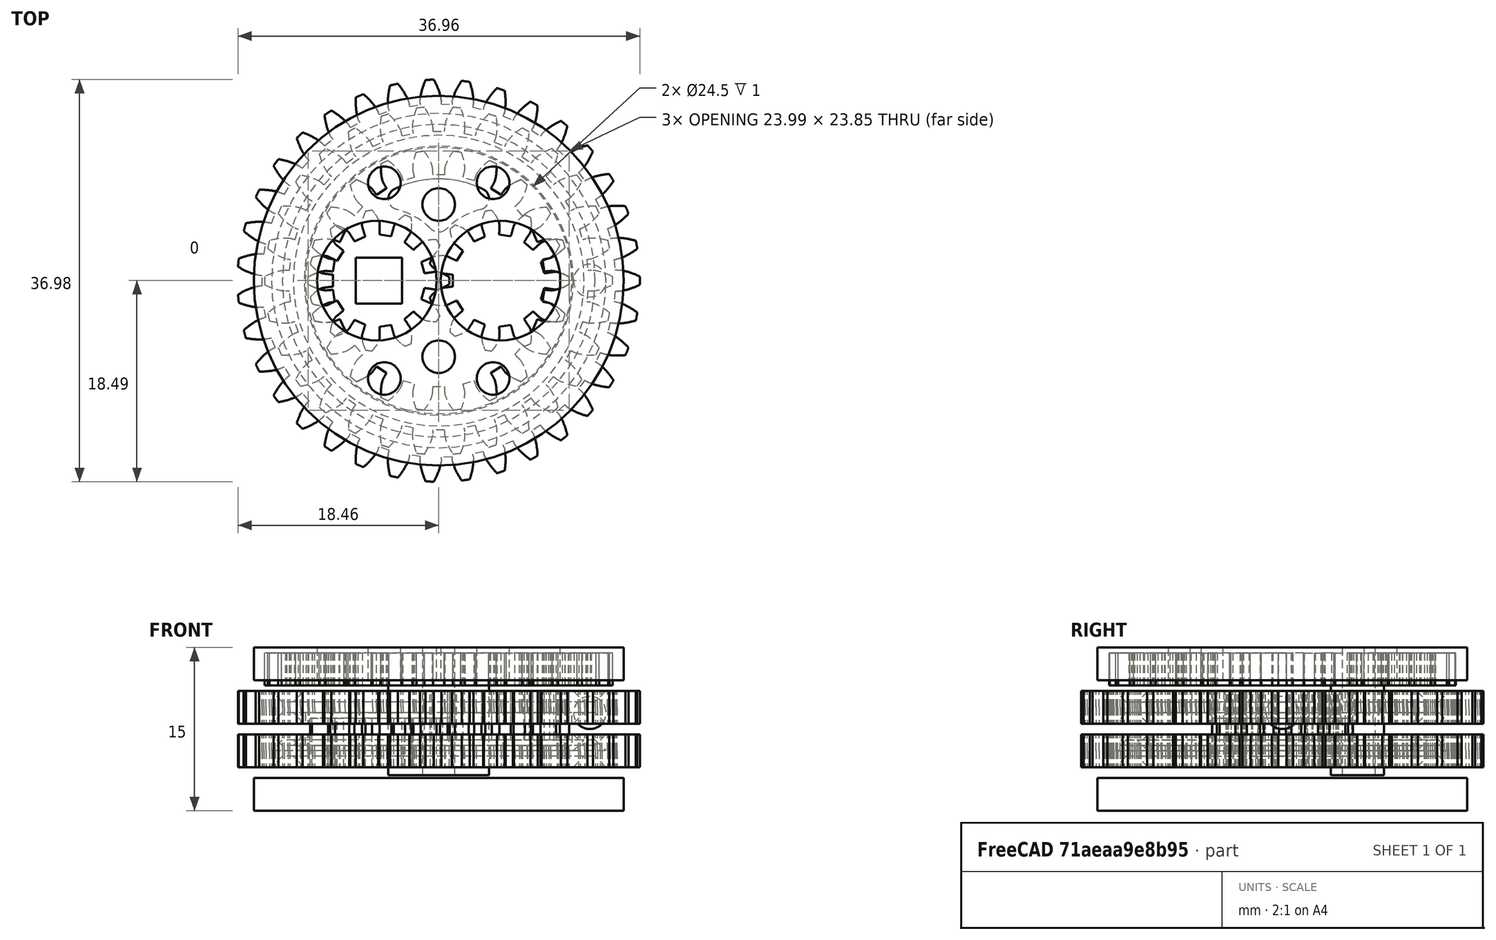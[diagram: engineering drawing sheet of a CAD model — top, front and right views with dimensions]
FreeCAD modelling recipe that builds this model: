
FCSTD DOCUMENT  (FreeCAD 0.16RUnknown)
Label: PlanetaryDifferential
License: CreativeCommons Attribution-NonCommercial
LicenseURL: http://creativecommons.org/licenses/by-nc/4.0/
objects: Sketcher::SketchObject×8, PartDesign::Pad×5, Part::FeaturePython×4, Part::Cut×4, PartDesign::Revolution×2, Part::Feature×2, Part::Sphere×1, Mesh::Feature×1, PartDesign::Fillet×1, Part::Mirroring×1, Part::MultiFuse×1
note: 36 computed .brp shape members not serialized (recipe doc carries the construction recipe); baked Part::Feature solids carry a one-line shape summary decoded from their .brp

FEATURE [Sketcher::SketchObject] Sketch
  sketch-geometry (3):
    g0: Circle CenterX=0 CenterY=0 CenterZ=0 NormalX=0 NormalY=0 NormalZ=1 Radius=36.0346
    g1: Circle CenterX=-36.0346 CenterY=0 CenterZ=0 NormalX=0 NormalY=0 NormalZ=1 Radius=36.0346
    g2: Circle CenterX=36.0346 CenterY=0 CenterZ=0 NormalX=0 NormalY=0 NormalZ=1 Radius=36.0346
  constraints (7):
    c: Coincident(g0,g-1)
    c: PointOnObject(g1,g0)
    c: PointOnObject(g2,g0)
    c: PointOnObject(g2,g-1)
    c: PointOnObject(g1,g-1)
    c: Equal(g0,g1)
    c: Equal(g1,g2)
FEATURE [Part::FeaturePython] InvoluteGear  # WARN: FeaturePython — macro-defined, semantics opaque (R4)
  backlash = 0
  beta = 0
  clearance = 0.25
  height = 5
  module = 1
  numpoints = 6
  pressure_angle = 20
  shift = 0
  simple = false
  teeth = 22
  undercut = false
FEATURE [Part::FeaturePython] InvoluteGear001  # WARN: FeaturePython — macro-defined, semantics opaque (R4)
  backlash = 0
  beta = 0
  clearance = 0.25
  height = 1.5
  module = 1
  numpoints = 6
  pressure_angle = 20
  shift = 0
  simple = false
  teeth = 35
  undercut = false
FEATURE [Part::Cut] Cut
  Base = -> InvoluteGear001
  Tool = -> InvoluteGear
FEATURE [Part::FeaturePython] InvoluteGear002  # WARN: FeaturePython — macro-defined, semantics opaque (R4)
  Placement = pos=(-5.5,0,-1.5) rot=(0,0,1;0rad)
  backlash = 0
  beta = 0
  clearance = 0.25
  height = 4.5
  module = 1
  numpoints = 6
  pressure_angle = 20
  shift = 0
  simple = false
  teeth = 11
  undercut = false
FEATURE [Part::FeaturePython] InvoluteGear003  # WARN: FeaturePython — macro-defined, semantics opaque (R4)
  Placement = pos=(5.5,0,1) rot=(0,0,1;0rad)
  backlash = 0
  beta = 0
  clearance = 0.25
  height = 4.5
  module = 1
  numpoints = 6
  pressure_angle = 20
  shift = 0
  simple = false
  teeth = 11
  undercut = false
FEATURE [Sketcher::SketchObject] Sketch001
  Placement = pos=(0,0,0) rot=(1,0,0;1.5708rad)
  sketch-geometry (13):
    g0: Circle [constr] CenterX=0 CenterY=2.26274 CenterZ=0 NormalX=0 NormalY=0 NormalZ=1 Radius=13.8736
    g1: Circle [constr] CenterX=13.5492 CenterY=-0.719672 CenterZ=0 NormalX=0 NormalY=0 NormalZ=1 Radius=1.5
    g2: Circle [constr] CenterX=13.8736 CenterY=2.26274 CenterZ=0 NormalX=0 NormalY=0 NormalZ=1 Radius=1.5
    g3: Circle [constr] CenterX=13.8736 CenterY=2.26274 CenterZ=0 NormalX=0 NormalY=0 NormalZ=1 Radius=1.6
    g4: LineSegment [constr] StartX=13.8736 StartY=2.26274 StartZ=0 EndX=13.4492 EndY=0.82402 EndZ=0
    g5: LineSegment [constr] StartX=13.4492 StartY=0.82402 StartZ=0 EndX=13.421 EndY=0.728105 EndZ=0
    g6: LineSegment [constr] StartX=0 StartY=2.26274 StartZ=0 EndX=13.8736 EndY=2.26274 EndZ=0
    g7: LineSegment StartX=12.3736 StartY=1.5 StartZ=0 EndX=13.3736 EndY=0.5 EndZ=0
    g8: LineSegment StartX=15.3736 StartY=1.5 StartZ=0 EndX=14.3736 EndY=0.5 EndZ=0
    g9: LineSegment StartX=13.3736 StartY=0.5 StartZ=0 EndX=14.3736 EndY=0.5 EndZ=0
    g10: LineSegment StartX=12.3736 StartY=1.5 StartZ=0 EndX=15.3736 EndY=1.5 EndZ=0
    g11: LineSegment [constr] StartX=13.8736 StartY=1.5 StartZ=0 EndX=13.8736 EndY=0.5 EndZ=0
    g12: LineSegment [constr] StartX=13.5492 StartY=-0.719672 StartZ=0 EndX=0 EndY=2.26274 EndZ=0
  constraints (34):
    c: PointOnObject(g1,g0)
    c: PointOnObject(g2,g0)
    c: Coincident(g3,g2)
    c: Tangent(g2,g1)
    c: Coincident(g4,g2)
    c: PointOnObject(g4,g2)
    c: Coincident(g4,g5)
    c: PointOnObject(g5,g3)
    c: Parallel(g5,g4)
    c: Distance(g5) = 0.1
    c: Radius(g2) = 1.5
    c: Equal(g2,g1)
    c: PointOnObject(g0,g-2)
    c: Coincident(g6,g0)
    c: Coincident(g6,g2)
    c: Horizontal(g6)
    c: Tangent(g7,g3)
    c: Coincident(g9,g7)
    c: Coincident(g9,g8)
    c: Tangent(g3,g8)
    c: Coincident(g10,g7)
    c: Coincident(g10,g8)
    c: PointOnObject(g11,g10)
    c: PointOnObject(g11,g9)
    c: Vertical(g11)
    c: Symmetric(g8,g7,g11)
    c: Symmetric(g7,g8,g11)
    c: DistanceY(g-1,g7) = 1.5
    c: DistanceY(g8,g8) = 1
    c: DistanceX(g10,g10) = 3
    c: DistanceX(g9,g9) = 1
    c: Coincident(g12,g1)
    c: Coincident(g12,g0)
    c: Angle(g12,g6) = 0.216662
FEATURE [Part::Sphere] Sphere
  Angle1 = -90
  Angle2 = 90
  Angle3 = 360
  Placement = pos=(13.9,0,3.5) rot=(0,0,1;0rad)
  Radius = 1.5
FEATURE [Sketcher::SketchObject] Sketch002
  Placement = pos=(0,0,-2.5) rot=(0,0,1;0rad)
  sketch-geometry (1):
    g0: Circle CenterX=0 CenterY=0 CenterZ=0 NormalX=0 NormalY=0 NormalZ=1 Radius=17
  constraints (2):
    c: Coincident(g0,g-1)
    c: Radius(g0) = 17
FEATURE [PartDesign::Pad] Pad
  Length = 3
  Length2 = 100
  Placement = pos=(0,0,-2.5) rot=(0,0,1;0rad)
  Reversed = true
  Sketch = -> Sketch002
  Type = 0
FEATURE [PartDesign::Revolution] Revolution
  Angle = 360
  Axis = (0,0,1)
  Base = (0,0,0)
  Placement = pos=(0,0,0) rot=(1,0,0;1.5708rad)
  ReferenceAxis = -> Sketch001 [V_Axis]
  Reversed = true
  Sketch = -> Sketch001
FEATURE [Sketcher::SketchObject] Sketch004
  Placement = pos=(-5.5,0,0) rot=(0,0,1;0rad)
  sketch-geometry (5):
    g0: LineSegment StartX=2.12132 StartY=2.12132 StartZ=0 EndX=-2.12132 EndY=2.12132 EndZ=0
    g1: LineSegment StartX=-2.12132 StartY=2.12132 StartZ=0 EndX=-2.12132 EndY=-2.12132 EndZ=0
    g2: LineSegment StartX=-2.12132 StartY=-2.12132 StartZ=0 EndX=2.12132 EndY=-2.12132 EndZ=0
    g3: LineSegment StartX=2.12132 StartY=-2.12132 StartZ=0 EndX=2.12132 EndY=2.12132 EndZ=0
    g4: Circle [constr] CenterX=0 CenterY=0 CenterZ=0 NormalX=0 NormalY=0 NormalZ=1 Radius=3
  constraints (14):
    c: Coincident(g0,g1)
    c: Coincident(g1,g2)
    c: Coincident(g2,g3)
    c: Coincident(g3,g0)
    c: Equal(g0,g1)
    c: Equal(g0,g2)
    c: Equal(g0,g3)
    c: PointOnObject(g0,g4)
    c: PointOnObject(g1,g4)
    c: PointOnObject(g2,g4)
    c: PointOnObject(g3,g4)
    c: Coincident(g4,g-1)
    c: Radius(g4) = 3
    c: Horizontal(g0)
FEATURE [PartDesign::Pad] Pad001
  Length = 30
  Length2 = 100
  Midplane = true
  Placement = pos=(-5.5,0,0) rot=(0,0,1;0rad)
  Sketch = -> Sketch004
  Type = 0
FEATURE [Sketcher::SketchObject] Sketch005
  Placement = pos=(0,0,6.5) rot=(0,0,1;0rad)
  sketch-geometry (9):
    g0: Circle CenterX=0 CenterY=0 CenterZ=0 NormalX=0 NormalY=0 NormalZ=1 Radius=17
    g1: Circle CenterX=5.68629 CenterY=0 CenterZ=0 NormalX=0 NormalY=0 NormalZ=1 Radius=5.5
    g2: Circle CenterX=-5.68629 CenterY=0 CenterZ=0 NormalX=0 NormalY=0 NormalZ=1 Radius=5.5
    g3: Circle CenterX=0 CenterY=7 CenterZ=0 NormalX=0 NormalY=0 NormalZ=1 Radius=1.5
    g4: Circle CenterX=0 CenterY=-7 CenterZ=0 NormalX=0 NormalY=0 NormalZ=1 Radius=1.5
    g5: Circle CenterX=5 CenterY=9 CenterZ=0 NormalX=0 NormalY=0 NormalZ=1 Radius=1.5
    g6: Circle CenterX=-5 CenterY=-9 CenterZ=0 NormalX=0 NormalY=0 NormalZ=1 Radius=1.5
    g7: Circle CenterX=-5 CenterY=9 CenterZ=0 NormalX=0 NormalY=0 NormalZ=1 Radius=1.5
    g8: Circle CenterX=5 CenterY=-9 CenterZ=0 NormalX=0 NormalY=0 NormalZ=1 Radius=1.5
  constraints (22):
    c: Coincident(g0,g-1)
    c: Radius(g0) = 17
    c: PointOnObject(g1,g-1)
    c: PointOnObject(g2,g-1)
    c: Symmetric(g2,g1,g-2)
    c: Radius(g2) = 5.5
    c: Equal(g2,g1)
    c: PointOnObject(g3,g-2)
    c: PointOnObject(g4,g-2)
    c: Symmetric(g4,g3,g-1)
    c: Radius(g3) = 1.5
    c: Equal(g3,g4)
    c: DistanceY(g4,g3) = 14
    c: Radius(g6) = 1.5
    c: Equal(g6,g5)
    c: Equal(g8,g7)
    c: Equal(g7,g5)
    c: Symmetric(g7,g5,g-2)
    c: Symmetric(g5,g8,g-1)
    c: Symmetric(g8,g6,g-2)
    c: DistanceY(g6,g7) = 18
    c: DistanceX(g7,g5) = 10
FEATURE [PartDesign::Pad] Pad002
  Length = 3
  Length2 = 100
  Placement = pos=(0,0,6.5) rot=(0,0,1;0rad)
  Sketch = -> Sketch005
  Type = 0
FEATURE [Mesh::Feature] DifferentialModel
  Placement = pos=(0,0,3) rot=(0,1,0;1.5708rad)
FEATURE [Part::Feature] Cut002  label="Cut"
  Placement = pos=(0,0,6) rot=(0,0,1;0rad)
  shape: bbox 31.99 x 31.89 x 3 mm, 314 faces (baked)
FEATURE [Sketcher::SketchObject] Sketch006
  sketch-geometry (4):
    g0: Circle CenterX=0 CenterY=7 CenterZ=0 NormalX=0 NormalY=0 NormalZ=1 Radius=1.5
    g1: ArcOfCircle CenterX=5.5 CenterY=0 CenterZ=0 NormalX=0 NormalY=0 NormalZ=1 Radius=6.75 StartAngle=1.41379 EndAngle=2.52321
    g2: ArcOfCircle CenterX=-5.5 CenterY=0 CenterZ=0 NormalX=0 NormalY=0 NormalZ=1 Radius=6.75 StartAngle=0.618387 EndAngle=1.7278
    g3: ArcOfCircle CenterX=0 CenterY=0 CenterZ=0 NormalX=0 NormalY=0 NormalZ=1 Radius=9.35 StartAngle=0.793832 EndAngle=2.34776
  constraints (14):
    c: PointOnObject(g0,g-2)
    c: PointOnObject(g1,g-1)
    c: PointOnObject(g1,g-2)
    c: PointOnObject(g2,g-1)
    c: Coincident(g2,g1)
    c: Coincident(g3,g-1)
    c: Coincident(g1,g3)
    c: Coincident(g2,g3)
    c: Radius(g0) = 1.5
    c: Symmetric(g2,g1,g-2)
    c: DistanceX(g2,g1) = 11
    c: Radius(g1) = 6.75
    c: Radius(g3) = 9.35
    c: DistanceY(g-1,g0) = 7
FEATURE [PartDesign::Pad] Pad003
  Length = 6.5
  Length2 = 2.25
  Sketch = -> Sketch006
  Type = 4
FEATURE [PartDesign::Fillet] Fillet
  Base = -> Pad003 [Edge1,Edge2,Edge5]
  Radius = 1
FEATURE [Sketcher::SketchObject] Sketch007
  Placement = pos=(0,0,0) rot=(1,0,0;1.5708rad)
  sketch-geometry (14):
    g0: Circle [constr] CenterX=0 CenterY=-0.762742 CenterZ=0 NormalX=0 NormalY=0 NormalZ=1 Radius=13.8736
    g1: Circle [constr] CenterX=13.5492 CenterY=-3.74516 CenterZ=0 NormalX=0 NormalY=0 NormalZ=1 Radius=1.5
    g2: Circle [constr] CenterX=13.8736 CenterY=-0.762742 CenterZ=0 NormalX=0 NormalY=0 NormalZ=1 Radius=1.5
    g3: Circle [constr] CenterX=13.8736 CenterY=-0.762742 CenterZ=0 NormalX=0 NormalY=0 NormalZ=1 Radius=1.6
    g4: LineSegment [constr] StartX=13.8736 StartY=-0.762742 StartZ=0 EndX=13.614 EndY=0.714628 EndZ=0
    g5: LineSegment [constr] StartX=13.614 StartY=0.714628 StartZ=0 EndX=13.5967 EndY=0.813119 EndZ=0
    g6: LineSegment [constr] StartX=0 StartY=-0.762742 StartZ=0 EndX=13.8736 EndY=-0.762742 EndZ=0
    g7: LineSegment [constr] StartX=13.8736 StartY=3 StartZ=0 EndX=13.8736 EndY=2 EndZ=0
    g8: LineSegment [constr] StartX=13.5492 StartY=-3.74516 StartZ=0 EndX=0 EndY=-0.762742 EndZ=0
    g9: LineSegment StartX=12.3736 StartY=0 StartZ=0 EndX=13.3736 EndY=1 EndZ=0
    g10: LineSegment StartX=13.3736 StartY=1 StartZ=0 EndX=14.3736 EndY=1 EndZ=0
    g11: LineSegment StartX=14.3736 StartY=1 StartZ=0 EndX=15.3736 EndY=0 EndZ=0
    g12: LineSegment StartX=15.3736 StartY=0 StartZ=0 EndX=12.3736 EndY=0 EndZ=0
    g13: LineSegment [constr] StartX=13.8736 StartY=1 StartZ=0 EndX=13.8736 EndY=0 EndZ=0
  constraints (35):
    c: PointOnObject(g1,g0)
    c: PointOnObject(g2,g0)
    c: Coincident(g3,g2)
    c: Tangent(g2,g1)
    c: Coincident(g4,g2)
    c: PointOnObject(g4,g2)
    c: Coincident(g4,g5)
    c: PointOnObject(g5,g3)
    c: Parallel(g5,g4)
    c: Distance(g5) = 0.1
    c: Radius(g2) = 1.5
    c: Equal(g2,g1)
    c: PointOnObject(g0,g-2)
    c: Coincident(g6,g0)
    c: Coincident(g6,g2)
    c: Horizontal(g6)
    c: Vertical(g7)
    c: Coincident(g8,g1)
    c: Coincident(g8,g0)
    c: Angle(g8,g6) = 0.216662
    c: Coincident(g9,g10)
    c: Coincident(g10,g11)
    c: Coincident(g11,g12)
    c: Coincident(g12,g9)
    c: PointOnObject(g13,g10)
    c: PointOnObject(g13,g12)
    c: Vertical(g13)
    c: Symmetric(g9,g10,g13)
    c: Symmetric(g9,g11,g13)
    c: PointOnObject(g9,g-1)
    c: Tangent(g3,g9)
    c: Tangent(g3,g11)
    c: Distance(g9,g11) = 3
    c: DistanceX(g10,g10) = 1
    c: DistanceY(g11,g10) = 1
FEATURE [PartDesign::Revolution] Revolution001
  Angle = 360
  Axis = (0,0,1)
  Base = (0,0,0)
  Placement = pos=(0,0,0) rot=(1,0,0;1.5708rad)
  ReferenceAxis = -> Sketch007 [V_Axis]
  Reversed = true
  Sketch = -> Sketch007
FEATURE [Part::Cut] Cut003002
  Base = -> Cut
  Tool = -> Revolution
FEATURE [Part::Mirroring] Part__Mirroring  label="Cut003002 (Mirror #1)"
  Base = (0,0,0)
  Normal = (0,0,1)
  Source = -> Cut003002
FEATURE [Part::MultiFuse] Fusion
  Shapes = -> [Cut003002,Part__Mirroring]
FEATURE [Sketcher::SketchObject] Sketch008
  Placement = pos=(0,0,1.5) rot=(0,0,1;0rad)
  sketch-geometry (1):
    g0: Circle CenterX=0 CenterY=0 CenterZ=0 NormalX=0 NormalY=0 NormalZ=1 Radius=12.25
  constraints (2):
    c: Coincident(g0,g-1)
    c: Radius(g0) = 12.25
FEATURE [PartDesign::Pad] Pad004
  Length = 1
  Length2 = 100
  Placement = pos=(0,0,1.5) rot=(0,0,1;0rad)
  Reversed = true
  Sketch = -> Sketch008
  Type = 0
FEATURE [Part::Cut] Cut003003
  Base = -> Fusion
  Tool = -> Pad004
FEATURE [Part::Feature] Cut003003001  label="Cut003003"
  Placement = pos=(0,0,4) rot=(1,0,0;3.14159rad)
  shape: bbox 36.95 x 36.99 x 3 mm, 639 faces (baked)
FEATURE [Part::Cut] Cut003003002
  Base = -> InvoluteGear002
  Tool = -> Pad001
